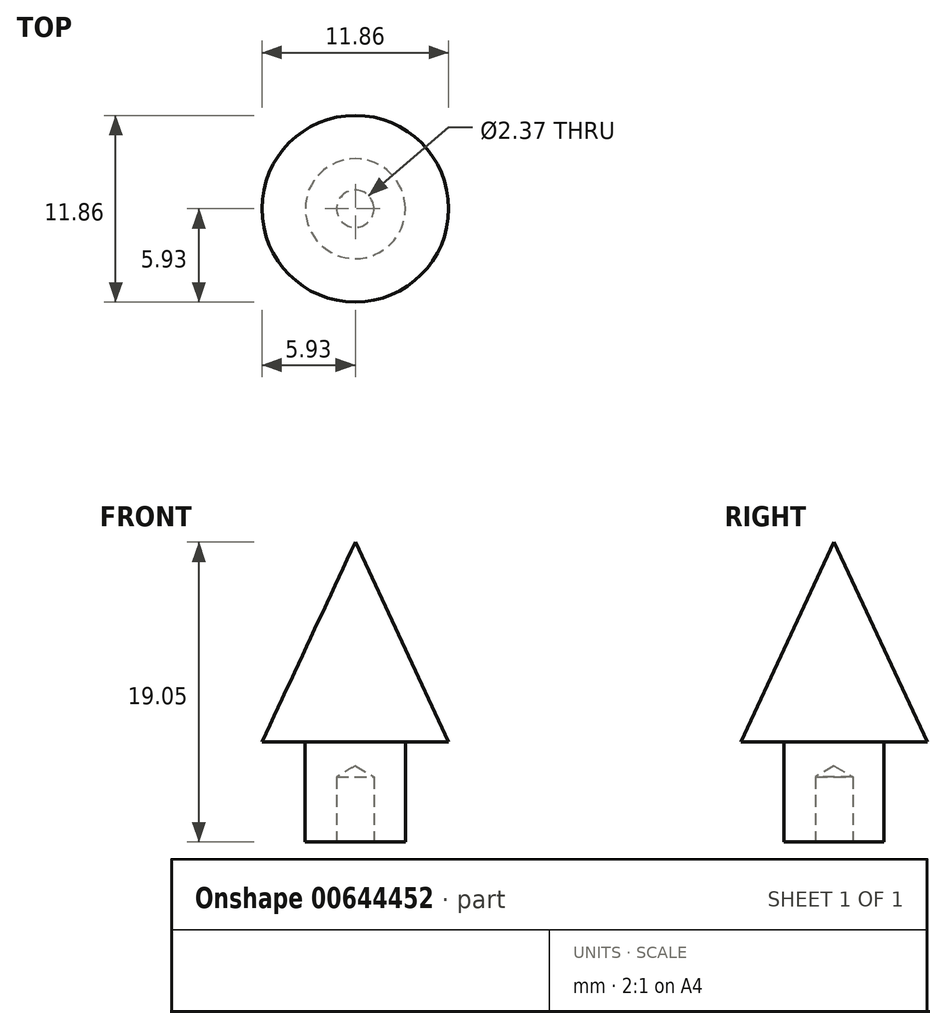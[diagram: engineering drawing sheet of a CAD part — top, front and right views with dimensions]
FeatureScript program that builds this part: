
annotation { "Feature Type Name" : "Feature", "Feature Type Description" : "" }
export const myFeature = defineFeature(function(context is Context, id is Id, definition is map)
    precondition{}
    {
        {
            var Q0;
            Q0=qCreatedBy(makeId("Front.planeOp"),FACE);
            var sketch = newSketch(context, id + "F0", { "sketchPlane" : qUnion([Q0])});
            skLineSegment(sketch, "E0", {"start": v(0, 0) * mm, "end": v(-3.18, 0) * mm});
            skLineSegment(sketch, "E1", {"start": v(-3.18, 0) * mm, "end": v(-3.18, 6.35) * mm});
            skLineSegment(sketch, "E2", {"start": v(-3.18, 6.35) * mm, "end": v(-5.93, 6.35) * mm});
            skLineSegment(sketch, "E3", {"start": v(-5.93, 6.35) * mm, "end": v(0, 19.05) * mm});
            skLineSegment(sketch, "E4", {"start": v(0, 19.05) * mm, "end": v(0, 0) * mm});
            skSolve(sketch);
        }
        {
            var Q0;
            Q0=makeQuery(id+"F0.imprint","IMPRINT",FACE,{"disambiguationData":[TD([[makeQuery(id+"F0.imprint","IMPRINT",EDGE,{"derivedFrom":sQuery(id+"F0.wireOp",EDGE,"E0")}),-1.0]])]});
            var Q1;
            Q1=sQuery(id+"F0.wireOp",EDGE,"E4");
            revolve(context, id + "F1", {"entities" : qUnion([Q0]), "axis" : qUnion([Q1]), "revolveType" : RevolveType.FULL});
        }
        {
            var Q0;
            Q0=makeQuery(id+"F1.opRevolve","SWEPT_FACE",FACE,{"disambiguationData":[OSD([sQuery(id+"F0.wireOp",EDGE,"E0")])]});
            var sketch = newSketch(context, id + "F2", { "sketchPlane" : qUnion([Q0])});
            skLineSegment(sketch, "E5", {"start": v(0, 0) * mm, "end": v(0, -3.18) * mm});
            skSolve(sketch);
        }
        {
            var Q0;
            Q0=sQuery(id+"F2.wireOp",VERTEX,"E5.start");
            var Q1;
            Q1=makeQuery(id+"F1.opRevolve","SWEPT_BODY",BODY,{"disambiguationData":[OSD([sQuery(id+"F0.wireOp",EDGE,"E0"),sQuery(id+"F0.wireOp",EDGE,"E1"),sQuery(id+"F0.wireOp",EDGE,"E2"),sQuery(id+"F0.wireOp",EDGE,"E3"),sQuery(id+"F0.wireOp",EDGE,"E4")])]});
            hole(context, id + "F3", {"style" : HoleStyle.SIMPLE, "endStyle" : HoleEndStyle.BLIND, "standardTappedOrClearance" : lookupTablePath({ "standard" : "ANSI", "engagement" : "75%", "pitch" : "48 tpi", "size" : "#4", "type" : "Tapped" }), "standardBlindInLast" : lookupTablePath({ "standard" : "ANSI", "engagement" : "75%", "pitch" : "48 tpi", "size" : "#4", "type" : "Tapped" }), "holeDiameter" : 2.37 * mm, "majorDiameter" : 2.84 * mm, "showTappedDepth" : true, "holeDepth" : 4.14 * mm, "isTappedThrough" : true, "tappedDepth" : 2.55 * mm, "tapClearance" : 3, "locations" : qUnion([Q0]), "scope" : qUnion([Q1])});
        }
    });
